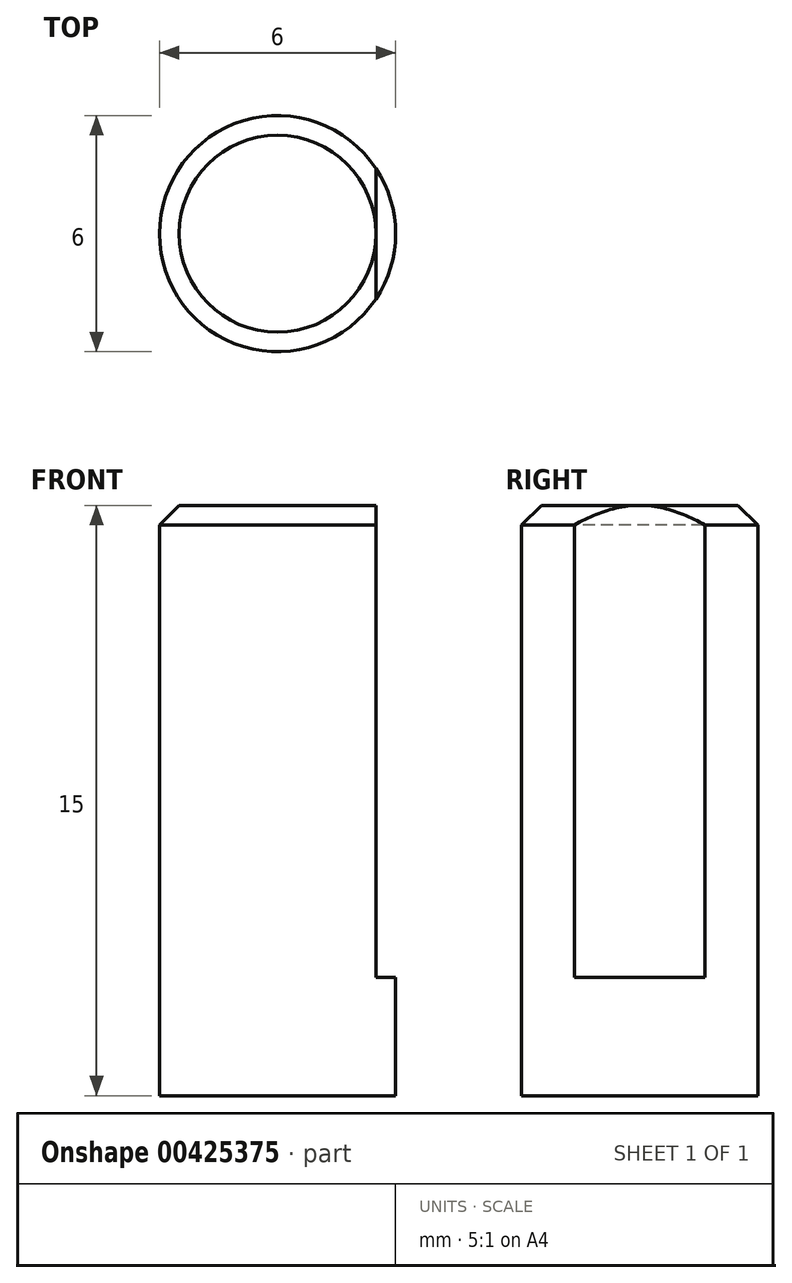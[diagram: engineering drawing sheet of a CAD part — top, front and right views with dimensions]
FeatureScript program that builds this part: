
annotation { "Feature Type Name" : "Feature", "Feature Type Description" : "" }
export const myFeature = defineFeature(function(context is Context, id is Id, definition is map)
    precondition{}
    {
        {
            var Q0;
            Q0=qCreatedBy(makeId("Top.planeOp"),FACE);
            var sketch = newSketch(context, id + "F0", { "sketchPlane" : qUnion([Q0])});
            skCircle(sketch, "E0", {"center": v(0, 0) * mm, "radius": 3 * mm});
            skSolve(sketch);
        }
        {
            var Q0;
            Q0 = qSketchRegion(id + "F0", true);
            extrude(context, id + "F1", {"entities" : qUnion([Q0]), "depth" : 15 * mm});
        }
        {
            var Q0;
            Q0=qCreatedBy(makeId("Right.planeOp"),FACE);
            cPlane(context, id + "F2", {"entities" : qUnion([Q0]), "cplaneType" : CPlaneType.OFFSET, "offset" : 2.5 * mm, "width" : 150 * mm, "height" : 150 * mm});
        }
        {
            var Q0;
            Q0=qCreatedBy(id+"F2.planeOp",FACE);
            var sketch = newSketch(context, id + "F3", { "sketchPlane" : qUnion([Q0])});
            skLineSegment(sketch, "E1.bottom", {"start": v(-4.82, 16.34) * mm, "end": v(5.3, 16.34) * mm});
            skLineSegment(sketch, "E1.top", {"start": v(-4.82, 3) * mm, "end": v(5.3, 3) * mm});
            skLineSegment(sketch, "E1.left", {"start": v(-4.82, 16.34) * mm, "end": v(-4.82, 3) * mm});
            skLineSegment(sketch, "E1.right", {"start": v(5.3, 16.34) * mm, "end": v(5.3, 3) * mm});
            skSolve(sketch);
        }
        {
            var Q0;
            Q0 = qSketchRegion(id + "F3", true);
            extrude(context, id + "F4", {"entities" : qUnion([Q0]), "operationType" : NewBodyOperationType.REMOVE, "depth" : 12 * mm});
        }
        {
            var Q0;
            Q0=makeQuery(id+"F1.opExtrude","CAP_EDGE",EDGE,{"disambiguationData":[OSD([sQuery(id+"F0.wireOp",EDGE,"E0")])],"isStart":false});
            chamfer(context, id + "F5", {"entities" : qUnion([Q0]), "width" : 0.5 * mm, "tangentPropagation" : true});
        }
    });
